# Revit family: NBS_Allermuir_OffcChrs-en-us-HavenBench_90ThreeWayUnit
name_source: partatom
category: Furniture
revit_build: Autodesk Revit 2018 (Build: 20190510_1515(x64)
units: mm (PartAtom-declared; Revit-internal decimal feet)

## family parameters
Always vertical = Yes
Cut with Voids When Loaded = No
Room Calculation Point = No
Shared = No
Work Plane-Based = No

## types (1)
- Haven_Bench_HAB3WC90
    AssetType = Movable
    BIMObjectName = NBS_Allermuir_OfficeChairs_Haven_Bench_HAB3WC90-US
    BenchMaterial = NBS_Allermuir_Fabric
    Category = Pr_40_50_12_57:Office chairs
    Description = 90° three way corner unit
    DurationUnit = year
    ExpectedLife = 10
    Features = Traditional carcass construction, Fully upholstered bench with quilted detail, Plastic glides, Linking device
    FeetMaterial = NBS_Allermuir_Plastic_Black
    Finish = Fully uplholstered
    IfcExportAs = IfcFurnitureType
    IfcExportType = BENCH
    IsBuiltIn = No
    ManufacturerName = Allermuir
    ManufacturerURL = www.allermuir.com
    ModelNumber = HAB3WC90
    ModelReference = Haven_Bench
    NBSCertification = www.nationalbimlibrary.com/cert/3ozauudp
    NBSDescription = Office chairs
    NBSReference = 45-35-20/330
    Name = OfficeChairs_HAB3WC90_Haven_Allermuir
    NominalDepth = 26 "
    NominalHeight = 18 "
    NominalLength = 30 "
    NominalWidth = 30 "
    OmniClassCode = 22-12 52 23
    OmniClassTitle = Office Seating
    OmniClassVersion = Table 22 2012-05-16
    ProductInformation = https://www.allermuir.com
    Size = 26 x 17.75 x 30"
    Status = UNSET
    Style = Corner unit
    Uniclass2015Code = Pr_40_50_12_57
    Uniclass2015Title = Office chairs
    Uniclass2015Version = Products v1.15
    Usage = Can be used individually or linked with others within the range
    Version = 1
    WarrantyDescription = Allermuir warrant that its manufactured products are free from manufacturing defects - in materials or workmanship - for a period of ten (10) years. , Allermuir will repair, or replace (at Allermuir's sole discretion) with comparable free of charge materials / components, any product / component which fails under normal use in a single shift environment, as a result of a defect in the materials and/ or workmanship
    WarrantyDurationParts = 10
    WarrantyDurationUnit = year

## geometry (parser evidence)
native form markers: Sweep x3
no freeform markers — native parametric forms only
